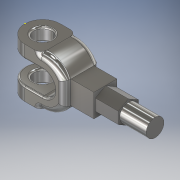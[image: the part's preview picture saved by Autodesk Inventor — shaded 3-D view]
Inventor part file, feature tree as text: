
AUTODESK INVENTOR PART (.ipt)
format: ipt  version: 2018 (Build 220112000, 112)  size: 257,536 bytes
history: native  units: in
note: dims shown in document units (in); Inventor stores cm internally (conversion verified against a paired STEP export)
features: sketch x8, extrude x6, fillet x4
ambient origin geometry x8: Origin, YZ Plane, XZ Plane, XY Plane, X Axis, Y Axis, Z Axis, Center Point
bodies: Solid1 (feature_tree)
feature tree (18):
  extrude  "Extrusion1"  Depth=1.5748in
  sketch  "Sketch2"  dims[d2=2.2047in d3=0.5906in d5=1.0236in]
  extrude  "Extrusion2"  Depth=0.5906in
  fillet  "Fillet1"  Radius=1.0236in
  sketch  "Sketch4"  dims[d8=1.5748in d9=0.0in d10=0.7874in d11=0.5118in]
  extrude  "Extrusion3"  Depth=2.6796in
  extrude  "Extrusion4"  Depth=0.7874in
  fillet  "Fillet2"  Radius=0.5118in
  extrude  "Extrusion5"  Depth=1.0236in TaperAngle=0.0deg
  extrude  "Extrusion6"  Depth=1.5748in
  fillet  "Fillet3"  Radius=1.0236in
  fillet  "Fillet4"  Radius=1.0236in
  sketch  "Sketch1"  dims[d0=0.5906in d1=1.5748in]
  sketch  "Sketch3"  dims[d6=3.5775in d7=2.6796in]
  sketch  "Sketch5"  dims[d12=0.5118in d13=1.0236in d14=0.0in]
  sketch  "Sketch6"  dims[d15=0.7874in d16=1.5748in d17=1.0236in d18=1.0236in d19=0.0in]
  sketch  "Sketch7"  dims[d20=1.0236in]
  sketch  "Sketch8"  dims[d21=1.0236in d22=0.0in d23=0.2756in d24=1.0236in d25=0.0in d26=0.7874in d27=1.1811in d28=0.0in d29=0.0787in d30=0.0787in]
